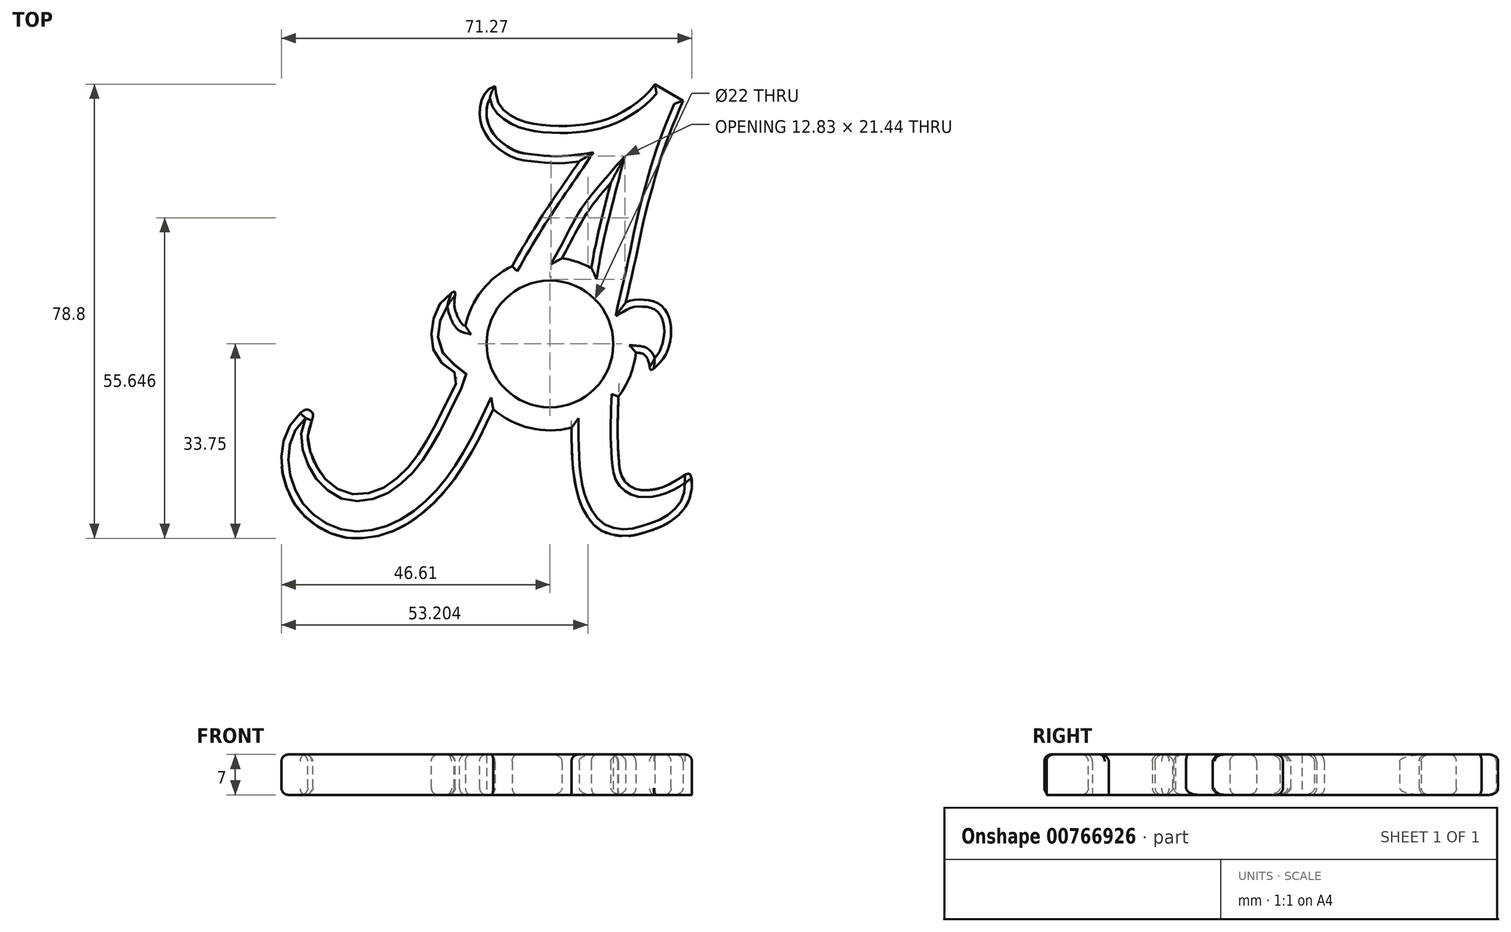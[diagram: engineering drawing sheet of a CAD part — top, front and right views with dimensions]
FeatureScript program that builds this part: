
annotation { "Feature Type Name" : "Feature", "Feature Type Description" : "" }
export const myFeature = defineFeature(function(context is Context, id is Id, definition is map)
    precondition{}
    {
        {
            var Q0;
            Q0=qCreatedBy(makeId("Top.planeOp"),FACE);
            var sketch = newSketch(context, id + "F0", { "sketchPlane" : qUnion([Q0])});
            skCircle(sketch, "E0", {"center": v(0, 0) * mm, "radius": 11 * mm});
            skArc(sketch, "E1.0", {"start": v(7.2, 13.16) * mm, "mid": v(4.73, 14.23) * mm, "end": v(2.1, 14.85) * mm});
            skFitSpline(sketch, "E2", {"points": [v(5.07, 31.67) * mm, v(-1.28, 22.3) * mm, v(-4.8, 16.56) * mm, v(-6.55, 13.5) * mm], "startDerivative": vector(-15.37, -22.85) * mm, "endDerivative": vector(-6.71, -11.99) * mm});
            skFitSpline(sketch, "E3", {"points": [v(2.1, 14.85) * mm, v(4.46, 19.25) * mm, v(6.68, 23.12) * mm, v(10.55, 27.92) * mm], "startDerivative": vector(7.4, 13.8) * mm, "endDerivative": vector(11.62, 13.48) * mm});
            skFitSpline(sketch, "E4", {"points": [v(10.55, 27.92) * mm, v(9.26, 22.88) * mm, v(7.85, 16.8) * mm, v(7.2, 13.16) * mm], "startDerivative": vector(-3.69, -14.15) * mm, "endDerivative": vector(-1.93, -11.75) * mm});
            skFitSpline(sketch, "E5", {"points": [v(5.07, 31.67) * mm, v(1.18, 31.35) * mm, v(-2.9, 31.67) * mm, v(-5.94, 32.17) * mm, v(-8.34, 33.45) * mm, v(-10.3, 35.18) * mm, v(-11.77, 37.61) * mm, v(-12.2, 39.66) * mm, v(-12.06, 41.57) * mm, v(-11.3, 43.47) * mm, v(-10.45, 44.32) * mm, v(-9.51, 44.7) * mm], "startDerivative": vector(-32.27, -4.3) * mm, "endDerivative": vector(16.4, 5.28) * mm});
            skFitSpline(sketch, "E6", {"points": [v(-9.51, 44.7) * mm, v(-9.2, 42.53) * mm, v(-8.4, 40.98) * mm, v(-6.88, 39.66) * mm, v(-4.83, 38.7) * mm, v(-2.2, 38.08) * mm, v(0.8, 37.82) * mm, v(4.54, 37.9) * mm, v(7.77, 38.37) * mm, v(11.1, 39.46) * mm, v(13.91, 41.04) * mm, v(15.4, 42.1) * mm, v(16.78, 43.32) * mm, v(18.22, 45.05) * mm], "startDerivative": vector(2.9, -31.73) * mm, "endDerivative": vector(19.51, 25.07) * mm});
            skFitSpline(sketch, "E7", {"points": [v(18.22, 45.05) * mm, v(23.1, 42.18) * mm], "startDerivative": vector(4.9, -2.87) * mm, "endDerivative": vector(4.9, -2.87) * mm});
            skFitSpline(sketch, "E8", {"points": [v(23.1, 42.18) * mm, v(20.51, 35.89) * mm, v(19.17, 31.99) * mm, v(17.73, 26.9) * mm, v(16.38, 21.92) * mm, v(15.22, 16.4) * mm, v(14.27, 12.02) * mm, v(13.17, 7.18) * mm], "startDerivative": vector(-17.4, -41.13) * mm, "endDerivative": vector(-8.14, -35.39) * mm});
            skFitSpline(sketch, "E9", {"points": [v(13.17, 7.18) * mm, v(14.02, 7.55) * mm, v(15.88, 7.67) * mm, v(18.32, 7.24) * mm, v(20.26, 5.55) * mm, v(21.02, 2.82) * mm, v(20.9, 0.63) * mm, v(20.26, -1.53) * mm, v(19.36, -2.93) * mm, v(17.54, -4.5) * mm, v(17.33, -4.05) * mm, v(17.12, -3.06) * mm, v(16.75, -2.27) * mm, v(16.05, -1.7) * mm, v(15.47, -1.57) * mm, v(14.92, -1.52) * mm], "startDerivative": vector(14.53, 7.9) * mm, "endDerivative": vector(-13.5, 1.18) * mm});
            skFitSpline(sketch, "E10", {"points": [v(11.9, -9.14) * mm, v(11.78, -12.62) * mm, v(11.78, -16.93) * mm, v(11.99, -20.57) * mm, v(12.46, -22.99) * mm, v(13.65, -24.47) * mm, v(15.22, -25.25) * mm, v(17.63, -25.32) * mm, v(20.06, -24.67) * mm, v(22.72, -23.18) * mm, v(24.16, -22.56) * mm, v(24.58, -23.4) * mm, v(24.62, -25) * mm, v(23.92, -27.66) * mm, v(22.38, -29.64) * mm, v(19.9, -31.42) * mm, v(16.75, -32.63) * mm, v(14.06, -33.29) * mm, v(11.33, -33.2) * mm, v(8.51, -32.14) * mm, v(6.48, -29.93) * mm, v(5.07, -27.04) * mm, v(4.13, -22.6) * mm, v(3.79, -17.76) * mm, v(3.75, -14.52) * mm], "startDerivative": vector(-2.45, -72.6) * mm, "endDerivative": vector(-0.35, 67.45) * mm});
            skFitSpline(sketch, "E11", {"points": [v(-9.83, -11.33) * mm, v(-11.39, -14.58) * mm, v(-13.63, -18.82) * mm, v(-16.04, -22.65) * mm, v(-18.8, -26.2) * mm, v(-21.7, -29.01) * mm, v(-24.76, -31.21) * mm, v(-27.94, -32.76) * mm, v(-30.5, -33.46) * mm, v(-33.65, -33.75) * mm, v(-36.38, -33.42) * mm, v(-38.58, -32.64) * mm, v(-40.86, -31.3) * mm, v(-43.5, -28.9) * mm, v(-45.3, -25.87) * mm, v(-46.32, -22.82) * mm, v(-46.6, -19.72) * mm, v(-46.04, -16.05) * mm, v(-44.57, -13.4) * mm, v(-42.86, -11.65) * mm, v(-42.16, -11.4) * mm, v(-41.6, -11.6) * mm, v(-41.14, -12.18) * mm, v(-41.4, -13.53) * mm, v(-41.84, -14.87) * mm, v(-42.04, -16.41) * mm, v(-41.67, -18.46) * mm, v(-40.74, -20.82) * mm, v(-39.23, -23.18) * mm, v(-37.96, -24.37) * mm, v(-36.05, -25.59) * mm, v(-33.65, -26.1) * mm, v(-30.7, -25.67) * mm, v(-28.18, -24.53) * mm, v(-26.02, -22.82) * mm, v(-24.07, -20.78) * mm, v(-21.38, -16.74) * mm, v(-18.85, -12.06) * mm, v(-17.22, -8.63) * mm, v(-15.7, -5.3) * mm, v(-16, -5.09) * mm, v(-16.8, -4.84) * mm, v(-18.03, -4.1) * mm, v(-19.46, -2.4) * mm, v(-20.36, -0.64) * mm, v(-20.6, 1.1) * mm, v(-20.44, 3.4) * mm, v(-19.95, 5.23) * mm, v(-19.21, 6.77) * mm, v(-18, 8.08) * mm, v(-16.57, 9.06) * mm, v(-16.44, 8.57) * mm, v(-16.57, 7.63) * mm, v(-16.57, 6.37) * mm, v(-16.24, 5.26) * mm, v(-15.8, 4.24) * mm, v(-15.14, 3.35) * mm, v(-14.67, 3.12) * mm], "startDerivative": vector(-66.54, -141.58) * mm, "endDerivative": vector(60.2, -15.46) * mm});
            skArc(sketch, "E12.trimOffspring", {"start": v(11.9, -9.14) * mm, "mid": v(13.94, -5.54) * mm, "end": v(14.92, -1.52) * mm});
            skArc(sketch, "E13.trimOffspring", {"start": v(-9.83, -11.33) * mm, "mid": v(-3.44, -14.6) * mm, "end": v(3.75, -14.52) * mm});
            skArc(sketch, "E14.trimOffspring", {"start": v(-6.55, 13.5) * mm, "mid": v(-11.8, 9.25) * mm, "end": v(-14.67, 3.12) * mm});
            skSolve(sketch);
        }
        {
            var Q0;
            Q0 = qSketchRegion(id + "F0", true);
            extrude(context, id + "F1", {"entities" : qUnion([Q0]), "depth" : 7 * mm, "offsetDistance" : 25 * mm});
        }
        {
            var Q0;
            Q0=makeQuery(id+"F1.opExtrude","CAP_EDGE",EDGE,{"disambiguationData":[OSD([sQuery(id+"F0.wireOp",EDGE,"E14.trimOffspring")])],"isStart":false});
            var Q1;
            Q1=makeQuery(id+"F1.opExtrude","CAP_EDGE",EDGE,{"disambiguationData":[OSD([sQuery(id+"F0.wireOp",EDGE,"E11")])],"isStart":false});
            var Q2;
            Q2=makeQuery(id+"F1.opExtrude","CAP_EDGE",EDGE,{"disambiguationData":[OSD([sQuery(id+"F0.wireOp",EDGE,"E13.trimOffspring")])],"isStart":false});
            var Q3;
            Q3=makeQuery(id+"F1.opExtrude","CAP_EDGE",EDGE,{"disambiguationData":[OSD([sQuery(id+"F0.wireOp",EDGE,"E10")])],"isStart":false});
            var Q4;
            Q4=makeQuery(id+"F1.opExtrude","CAP_EDGE",EDGE,{"disambiguationData":[OSD([sQuery(id+"F0.wireOp",EDGE,"E12.trimOffspring")])],"isStart":false});
            var Q5;
            Q5=makeQuery(id+"F1.opExtrude","CAP_EDGE",EDGE,{"disambiguationData":[OSD([sQuery(id+"F0.wireOp",EDGE,"E9")])],"isStart":false});
            var Q6;
            Q6=makeQuery(id+"F1.opExtrude","CAP_EDGE",EDGE,{"disambiguationData":[OSD([sQuery(id+"F0.wireOp",EDGE,"E8")])],"isStart":false});
            var Q7;
            Q7=makeQuery(id+"F1.opExtrude","CAP_EDGE",EDGE,{"disambiguationData":[OSD([sQuery(id+"F0.wireOp",EDGE,"E2")])],"isStart":false});
            var Q8;
            Q8=makeQuery(id+"F1.opExtrude","CAP_EDGE",EDGE,{"disambiguationData":[OSD([sQuery(id+"F0.wireOp",EDGE,"E3")])],"isStart":false});
            var Q9;
            Q9=makeQuery(id+"F1.opExtrude","CAP_EDGE",EDGE,{"disambiguationData":[OSD([sQuery(id+"F0.wireOp",EDGE,"E4")])],"isStart":false});
            var Q10;
            Q10=makeQuery(id+"F1.opExtrude","CAP_EDGE",EDGE,{"disambiguationData":[OSD([sQuery(id+"F0.wireOp",EDGE,"E1.0")])],"isStart":false});
            var Q11;
            Q11=makeQuery(id+"F1.opExtrude","CAP_EDGE",EDGE,{"disambiguationData":[OSD([sQuery(id+"F0.wireOp",EDGE,"E7")])],"isStart":false});
            var Q12;
            Q12=makeQuery(id+"F1.opExtrude","CAP_EDGE",EDGE,{"disambiguationData":[OSD([sQuery(id+"F0.wireOp",EDGE,"E5")])],"isStart":false});
            var Q13;
            Q13=makeQuery(id+"F1.opExtrude","CAP_EDGE",EDGE,{"disambiguationData":[OSD([sQuery(id+"F0.wireOp",EDGE,"E6")])],"isStart":false});
            var Q14;
            Q14=makeQuery(id+"F1.opExtrude","CAP_EDGE",EDGE,{"disambiguationData":[OSD([sQuery(id+"F0.wireOp",EDGE,"E8")])],"isStart":true});
            var Q15;
            Q15=makeQuery(id+"F1.opExtrude","CAP_EDGE",EDGE,{"disambiguationData":[OSD([sQuery(id+"F0.wireOp",EDGE,"E7")])],"isStart":true});
            var Q16;
            Q16=makeQuery(id+"F1.opExtrude","CAP_EDGE",EDGE,{"disambiguationData":[OSD([sQuery(id+"F0.wireOp",EDGE,"E6")])],"isStart":true});
            var Q17;
            Q17=makeQuery(id+"F1.opExtrude","CAP_EDGE",EDGE,{"disambiguationData":[OSD([sQuery(id+"F0.wireOp",EDGE,"E5")])],"isStart":true});
            var Q18;
            Q18=makeQuery(id+"F1.opExtrude","CAP_EDGE",EDGE,{"disambiguationData":[OSD([sQuery(id+"F0.wireOp",EDGE,"E2")])],"isStart":true});
            var Q19;
            Q19=makeQuery(id+"F1.opExtrude","CAP_EDGE",EDGE,{"disambiguationData":[OSD([sQuery(id+"F0.wireOp",EDGE,"E3")])],"isStart":true});
            var Q20;
            Q20=makeQuery(id+"F1.opExtrude","CAP_EDGE",EDGE,{"disambiguationData":[OSD([sQuery(id+"F0.wireOp",EDGE,"E4")])],"isStart":true});
            var Q21;
            Q21=makeQuery(id+"F1.opExtrude","CAP_EDGE",EDGE,{"disambiguationData":[OSD([sQuery(id+"F0.wireOp",EDGE,"E1.0")])],"isStart":true});
            var Q22;
            Q22=makeQuery(id+"F1.opExtrude","CAP_EDGE",EDGE,{"disambiguationData":[OSD([sQuery(id+"F0.wireOp",EDGE,"E14.trimOffspring")])],"isStart":true});
            var Q23;
            Q23=makeQuery(id+"F1.opExtrude","CAP_EDGE",EDGE,{"disambiguationData":[OSD([sQuery(id+"F0.wireOp",EDGE,"E11")])],"isStart":true});
            var Q24;
            Q24=makeQuery(id+"F1.opExtrude","CAP_EDGE",EDGE,{"disambiguationData":[OSD([sQuery(id+"F0.wireOp",EDGE,"E13.trimOffspring")])],"isStart":true});
            var Q25;
            Q25=makeQuery(id+"F1.opExtrude","CAP_EDGE",EDGE,{"disambiguationData":[OSD([sQuery(id+"F0.wireOp",EDGE,"E12.trimOffspring")])],"isStart":true});
            var Q26;
            Q26=makeQuery(id+"F1.opExtrude","CAP_EDGE",EDGE,{"disambiguationData":[OSD([sQuery(id+"F0.wireOp",EDGE,"E9")])],"isStart":true});
            fillet(context, id + "F2", {"entities" : qUnion([Q0, Q1, Q2, Q3, Q4, Q5, Q6, Q7, Q8, Q9, Q10, Q11, Q12, Q13, Q14, Q15, Q16, Q17, Q18, Q19, Q20, Q21, Q22, Q23, Q24, Q25, Q26]), "radius" : 1.2 * mm, "tangentPropagation" : true, "allowEdgeOverflow" : false});
        }
    });
